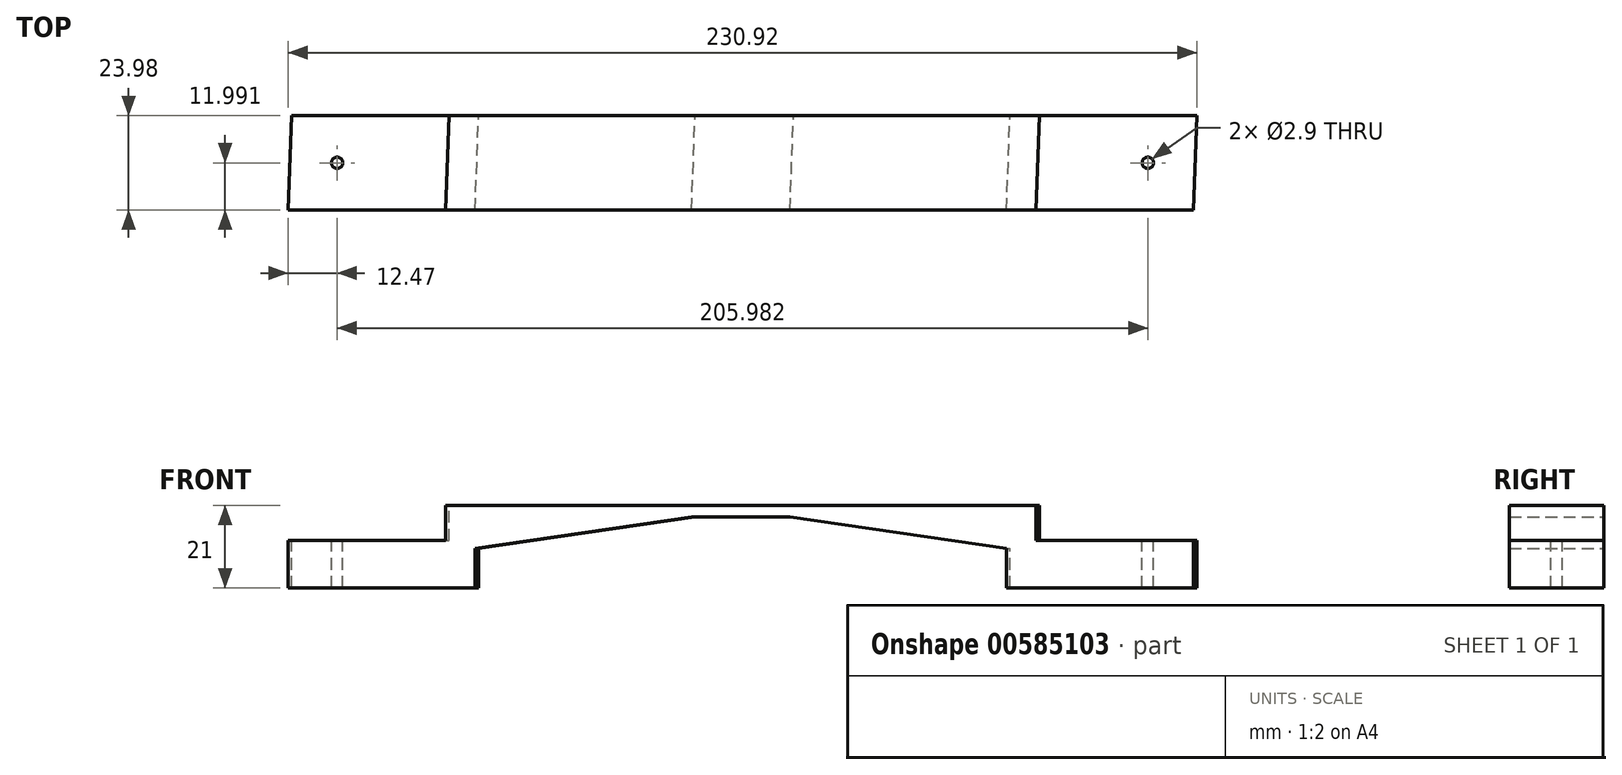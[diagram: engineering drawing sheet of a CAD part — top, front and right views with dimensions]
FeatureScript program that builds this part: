
annotation { "Feature Type Name" : "Feature", "Feature Type Description" : "" }
export const myFeature = defineFeature(function(context is Context, id is Id, definition is map)
    precondition{}
    {
        {
            var Q0;
            Q0=qCreatedBy(makeId("Front.planeOp"),FACE);
            var sketch = newSketch(context, id + "F0", { "sketchPlane" : qUnion([Q0])});
            skLineSegment(sketch, "E0", {"start": v(-40, 0) * mm, "end": v(0, 0) * mm});
            skLineSegment(sketch, "E1", {"start": v(0, 0) * mm, "end": v(0, 9) * mm});
            skLineSegment(sketch, "E2", {"start": v(0, 9) * mm, "end": v(150, 9) * mm});
            skLineSegment(sketch, "E3", {"start": v(150, 9) * mm, "end": v(150, 0) * mm});
            skLineSegment(sketch, "E4", {"start": v(150, 0) * mm, "end": v(190, 0) * mm});
            skLineSegment(sketch, "E5", {"start": v(190, 0) * mm, "end": v(190, -12) * mm});
            skLineSegment(sketch, "E6", {"start": v(190, -12) * mm, "end": v(142.5, -12) * mm});
            skLineSegment(sketch, "E7", {"start": v(142.5, -12) * mm, "end": v(142.5, -2) * mm});
            skLineSegment(sketch, "E8", {"start": v(87.5, 6) * mm, "end": v(62.5, 6) * mm});
            skLineSegment(sketch, "E9", {"start": v(7.5, -2) * mm, "end": v(7.5, -12) * mm});
            skLineSegment(sketch, "E10", {"start": v(7.5, -12) * mm, "end": v(-40, -12) * mm});
            skLineSegment(sketch, "E11", {"start": v(-40, -12) * mm, "end": v(-40, 0) * mm});
            skLineSegment(sketch, "E12", {"start": v(7.5, -2) * mm, "end": v(62.5, 6) * mm});
            skLineSegment(sketch, "E13", {"start": v(87.5, 6) * mm, "end": v(142.5, -2) * mm});
            skLineSegment(sketch, "E14", {"start": v(75, 6) * mm, "end": v(75, 9) * mm, "construction": true});
            skPoint(sketch, "E14.endSnap0", {"position": v(75, 9) * mm});
            skSolve(sketch);
        }
        {
            var Q0;
            Q0=qCreatedBy(makeId("Top.planeOp"),FACE);
            var sketch = newSketch(context, id + "F1", { "sketchPlane" : qUnion([Q0])});
            skLineSegment(sketch, "E15", {"start": v(-39.08, 23.98) * mm, "end": v(-40, 0) * mm});
            skLineSegment(sketch, "E16", {"start": v(-40, 0) * mm, "end": v(-40, 16.3) * mm, "construction": true});
            skSolve(sketch);
        }
        {
            var Q0;
            Q0 = qSketchRegion(id + "F0", true);
            var Q1;
            Q1=sQuery(id+"F1.wireOp",EDGE,"E15");
            sweep(context, id + "F2", {"profiles" : qUnion([Q0]), "path" : qUnion([Q1])});
        }
        {
            var Q0;
            Q0=makeQuery(id+"F2.opSweep","SWEPT_FACE",FACE,{"disambiguationData":[OSD([sQuery(id+"F0.wireOp",EDGE,"E0"),sQuery(id+"F1.wireOp",EDGE,"E15")])]});
            var sketch = newSketch(context, id + "F3", { "sketchPlane" : qUnion([Q0])});
            skCircle(sketch, "E17", {"center": v(178.45, 12) * mm, "radius": 1.45 * mm});
            skLineSegment(sketch, "E18", {"start": v(-29.07, -28) * mm, "end": v(-26, 52) * mm, "construction": true});
            skLineSegment(sketch, "E19", {"start": v(179.99, 52) * mm, "end": v(176.92, -28) * mm, "construction": true});
            skCircle(sketch, "E20", {"center": v(-27.53, 12) * mm, "radius": 1.45 * mm});
            skLineSegment(sketch, "E21", {"start": v(-39.54, 12) * mm, "end": v(-27.53, 12) * mm, "construction": true});
            skLineSegment(sketch, "E22", {"start": v(-27.53, 12) * mm, "end": v(178.45, 12) * mm, "construction": true});
            skSolve(sketch);
        }
        {
            var Q0;
            Q0 = qSketchRegion(id + "F3", true);
            extrude(context, id + "F4", {"entities" : qUnion([Q0]), "operationType" : NewBodyOperationType.REMOVE, "endBound" : BoundingType.UP_TO_NEXT, "oppositeDirection" : true, "depth" : 25 * mm, "offsetDistance" : 25 * mm});
        }
    });
